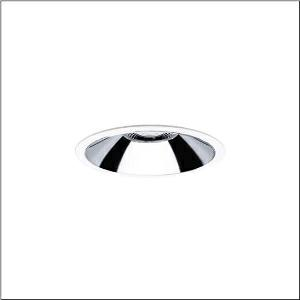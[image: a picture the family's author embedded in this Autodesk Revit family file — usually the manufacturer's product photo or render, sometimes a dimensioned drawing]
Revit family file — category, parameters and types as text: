
# Revit family: lunis_21_xl_51db15df33
name_source: partatom
category: Lighting Fixtures
units: mm (PartAtom-declared; Revit-internal decimal feet)

## family parameters
Cut with Voids When Loaded = No
Host = Face
Light Source = No
Part Type = Normal
Room Calculation Point = No
Round Connector Dimension = Use Diameter
Shared = No

## types (1)
- Lunis 21 XL (1 x LED, 3360 lm, 31 W, 3000K)
    Apparent Load = 31 VA
    CIE Flux Codes = 89 99 100 100 100
    Color Rendering = 80
    Color Temperature = 3000K
    Default Elevation = 1800 mm
    Description = Lunis 21,  XL, downlight, of PC, light emission: direct distribution, LED rated luminous flux: 3.360lm, light colour: 830, control gear: ECG DALI, with terminal, 5-pole, mains connection: 220..240V, AC, housing, round, of diecast aluminium, traffic white (RAL 9016), diameter: 213mm, protection rating (complete): IP20, protection rating (on room side): IP54, insulation class (complete): insulation class II (safety insulation), certification: CE, impact resistance: IK02, packaging unit: 1 piece
    Height = 0 mm  [stored 0 ft]
    Lamp = 1 x LED
    Lamp Light Flux = 3360 lm
    Lamp Power = 31 W
    Lamp count = 1
    Length = 213 mm
    Luminous efficacy = 108 lm/W
    Manufacturer = Siteco
    ModVariant = No
    Model = 51DB15DF33
    Mounting Place = Ceiling
    Mounting Type = Recessed
    Number of Poles = 1
    OnlyDefault = Yes
    Power Factor = 1
    Product Name = Lunis 21 XL
    Product group = downlight
    ProductGroupID = 400
    Protection Class = Protection class II
    Protection Degree = IP 20
    RLX_Detail_Level = 1
    RLX_Emergency_Light_Flux = 0 lm
    RLX_Emergency_Type = 0
    RLX_Emergency_Type_DB = No
    RlxData = <blob elided: 26945 chars, md5=b3c51fcd>
    Socket = socket
    Standby Power = 0 W
    System Light Flux = 3360 lm
    System Power = 31 W
    Type Comments = Product without accessories
    Type Image = l_1287385.jpg
    URL = http://relux.com
    VarID = ---
    Voltage = 0 V
    Weight = 0.00 kg
    Width = 0 mm  [stored 0 ft]

note: [stored X ft] marks values corroborated as IEEE doubles in the binary element streams (Revit-internal decimal feet)

## geometry (parser evidence)
native form markers: Blend x4, Sweep x13
no freeform markers — native parametric forms only
